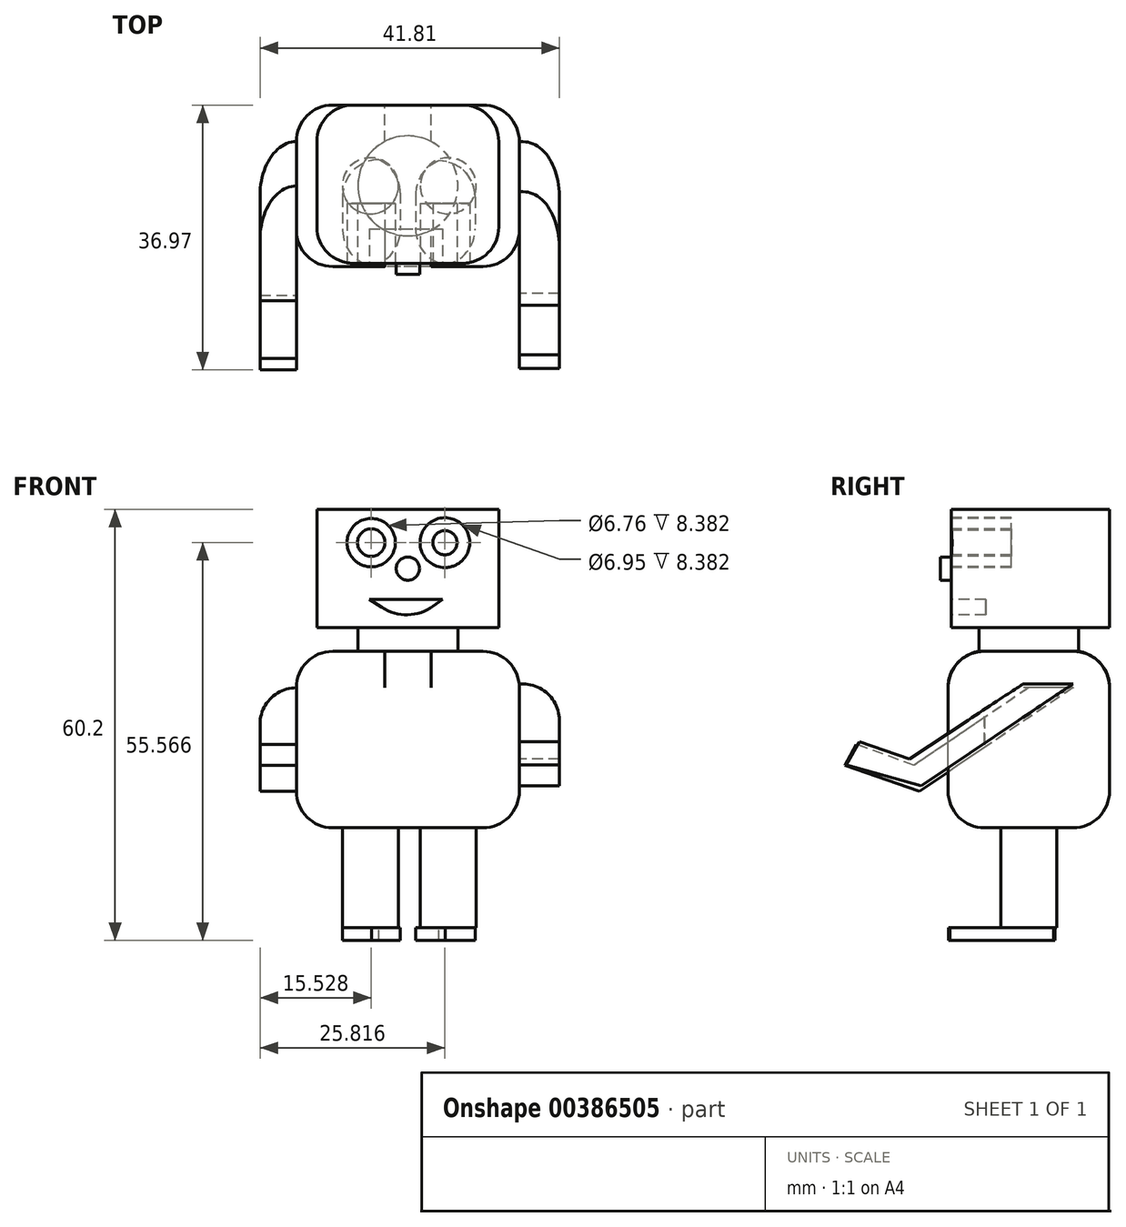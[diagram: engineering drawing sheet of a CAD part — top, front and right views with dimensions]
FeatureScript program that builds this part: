
annotation { "Feature Type Name" : "Feature", "Feature Type Description" : "" }
export const myFeature = defineFeature(function(context is Context, id is Id, definition is map)
    precondition{}
    {
        {
            var Q0;
            Q0=qCreatedBy(makeId("Front.planeOp"),FACE);
            var sketch = newSketch(context, id + "F0", { "sketchPlane" : qUnion([Q0])});
            skLineSegment(sketch, "E0.bottom", {"start": v(12.7, -8.26) * mm, "end": v(-12.7, -8.26) * mm});
            skLineSegment(sketch, "E0.top", {"start": v(12.7, 8.26) * mm, "end": v(-12.7, 8.26) * mm});
            skLineSegment(sketch, "E0.left", {"start": v(12.7, -8.26) * mm, "end": v(12.7, 8.26) * mm});
            skLineSegment(sketch, "E0.right", {"start": v(-12.7, -8.26) * mm, "end": v(-12.7, 8.26) * mm});
            skPoint(sketch, "E0.middle", {"position": v(0, 0) * mm});
            skSolve(sketch);
        }
        {
            var Q0;
            Q0 = qSketchRegion(id + "F0", true);
            extrude(context, id + "F1", {"entities" : qUnion([Q0]), "depth" : 22.1 * mm});
        }
        {
            var Q0;
            Q0=makeQuery(id+"F1.opExtrude","CAP_EDGE",EDGE,{"disambiguationData":[OSD([sQuery(id+"F0.wireOp",EDGE,"E0.right")])],"isStart":false});
            var Q1;
            Q1=makeQuery(id+"F1.opExtrude","CAP_EDGE",EDGE,{"disambiguationData":[OSD([sQuery(id+"F0.wireOp",EDGE,"E0.left")])],"isStart":false});
            var Q2;
            Q2=makeQuery(id+"F1.opExtrude","CAP_EDGE",EDGE,{"disambiguationData":[OSD([sQuery(id+"F0.wireOp",EDGE,"E0.right")])],"isStart":true});
            var Q3;
            Q3=makeQuery(id+"F1.opExtrude","CAP_EDGE",EDGE,{"disambiguationData":[OSD([sQuery(id+"F0.wireOp",EDGE,"E0.left")])],"isStart":true});
            fillet(context, id + "F2", {"entities" : qUnion([Q0, Q1, Q2, Q3]), "radius" : 5.08 * mm, "tangentPropagation" : true, "allowEdgeOverflow" : false});
        }
        {
            var Q0;
            Q0=makeQuery(id+"F1.opExtrude","SWEPT_FACE",FACE,{"disambiguationData":[OSD([sQuery(id+"F0.wireOp",EDGE,"E0.bottom")])]});
            var sketch = newSketch(context, id + "F3", { "sketchPlane" : qUnion([Q0])});
            skCircle(sketch, "E1", {"center": v(0, 11.27) * mm, "radius": 6.98 * mm});
            skSolve(sketch);
        }
        {
            var Q0;
            Q0 = qSketchRegion(id + "F3", true);
            extrude(context, id + "F4", {"entities" : qUnion([Q0]), "operationType" : NewBodyOperationType.ADD, "depth" : 3.3 * mm});
        }
        {
            var Q0;
            Q0=makeQuery(id+"F4.opExtrude","CAP_FACE",FACE,{"disambiguationData":[OSD([sQuery(id+"F3.wireOp",EDGE,"E1")])],"isStart":false});
            var sketch = newSketch(context, id + "F5", { "sketchPlane" : qUnion([Q0])});
            skLineSegment(sketch, "E2.bottom", {"start": v(15.57, 0) * mm, "end": v(-15.57, 0) * mm});
            skLineSegment(sketch, "E2.top", {"start": v(15.57, 22.55) * mm, "end": v(-15.57, 22.55) * mm});
            skLineSegment(sketch, "E2.left", {"start": v(15.57, 0) * mm, "end": v(15.57, 22.55) * mm});
            skLineSegment(sketch, "E2.right", {"start": v(-15.57, 0) * mm, "end": v(-15.57, 22.55) * mm});
            skPoint(sketch, "E2.middle", {"position": v(0, 11.27) * mm});
            skSolve(sketch);
        }
        {
            var Q0;
            Q0 = qSketchRegion(id + "F5", true);
            extrude(context, id + "F6", {"entities" : qUnion([Q0]), "operationType" : NewBodyOperationType.ADD, "depth" : 24.64 * mm});
        }
        {
            var Q0;
            Q0=makeQuery(id+"F6.opExtrude","SWEPT_EDGE",EDGE,{"disambiguationData":[OSD([sQuery(id+"F5.wireOp",EDGE,"E2.top"),sQuery(id+"F5.wireOp",EDGE,"E2.left")])]});
            var Q1;
            Q1=makeQuery(id+"F6.opExtrude","SWEPT_EDGE",EDGE,{"disambiguationData":[OSD([sQuery(id+"F5.wireOp",EDGE,"E2.top"),sQuery(id+"F5.wireOp",EDGE,"E2.right")])]});
            var Q2;
            Q2=makeQuery(id+"F6.opExtrude","SWEPT_EDGE",EDGE,{"disambiguationData":[OSD([sQuery(id+"F5.wireOp",EDGE,"E2.bottom"),sQuery(id+"F5.wireOp",EDGE,"E2.left")])]});
            var Q3;
            Q3=makeQuery(id+"F6.opExtrude","SWEPT_EDGE",EDGE,{"disambiguationData":[OSD([sQuery(id+"F5.wireOp",EDGE,"E2.bottom"),sQuery(id+"F5.wireOp",EDGE,"E2.right")])]});
            var Q4;
            Q4=makeQuery(id+"F6.opExtrude","CAP_EDGE",EDGE,{"disambiguationData":[OSD([sQuery(id+"F5.wireOp",EDGE,"E2.left")])],"isStart":true});
            var Q5;
            Q5=makeQuery(id+"F6.opExtrude","CAP_EDGE",EDGE,{"disambiguationData":[OSD([sQuery(id+"F5.wireOp",EDGE,"E2.bottom")])],"isStart":true});
            var Q6;
            Q6=makeQuery(id+"F6.opExtrude","SWEPT_FACE",FACE,{"disambiguationData":[OSD([sQuery(id+"F5.wireOp",EDGE,"E2.top")])]});
            var Q7;
            Q7=makeQuery(id+"F6.opExtrude","CAP_EDGE",EDGE,{"disambiguationData":[OSD([sQuery(id+"F5.wireOp",EDGE,"E2.top")])],"isStart":false});
            var Q8;
            Q8=makeQuery(id+"F6.opExtrude","CAP_EDGE",EDGE,{"disambiguationData":[OSD([sQuery(id+"F5.wireOp",EDGE,"E2.right")])],"isStart":false});
            var Q9;
            Q9=makeQuery(id+"F6.opExtrude","CAP_EDGE",EDGE,{"disambiguationData":[OSD([sQuery(id+"F5.wireOp",EDGE,"E2.bottom")])],"isStart":false});
            var Q10;
            Q10=makeQuery(id+"F6.opExtrude","CAP_EDGE",EDGE,{"disambiguationData":[OSD([sQuery(id+"F5.wireOp",EDGE,"E2.left")])],"isStart":false});
            var Q11;
            Q11=makeQuery(id+"F6.opExtrude","CAP_EDGE",EDGE,{"disambiguationData":[OSD([sQuery(id+"F5.wireOp",EDGE,"E2.right")])],"isStart":true});
            fillet(context, id + "F7", {"entities" : qUnion([Q0, Q1, Q2, Q3, Q4, Q5, Q6, Q7, Q8, Q9, Q10, Q11]), "radius" : 5.08 * mm, "tangentPropagation" : true, "allowEdgeOverflow" : false});
        }
        {
            var Q0;
            Q0=makeQuery(id+"F6.opExtrude","SWEPT_FACE",FACE,{"disambiguationData":[OSD([sQuery(id+"F5.wireOp",EDGE,"E2.left")])]});
            var sketch = newSketch(context, id + "F8", { "sketchPlane" : qUnion([Q0])});
            skLineSegment(sketch, "E3", {"start": v(-11.27, -16.64) * mm, "end": v(-27.42, -27.24) * mm});
            skLineSegment(sketch, "E4", {"start": v(-5.08, -16.64) * mm, "end": v(-27.13, -31.12) * mm});
            skSolve(sketch);
        }
        {
            var Q0;
            Q0=makeQuery(id+"F6.opExtrude","SWEPT_FACE",FACE,{"disambiguationData":[OSD([sQuery(id+"F5.wireOp",EDGE,"E2.right")])]});
            var sketch = newSketch(context, id + "F9", { "sketchPlane" : qUnion([Q0])});
            skLineSegment(sketch, "E5", {"start": v(11.27, -16.64) * mm, "end": v(27.3, -27.49) * mm});
            skLineSegment(sketch, "E6", {"start": v(5.08, -16.64) * mm, "end": v(26.53, -31.11) * mm});
            skLineSegment(sketch, "E7", {"start": v(27.3, -27.49) * mm, "end": v(35.36, -24.53) * mm});
            skLineSegment(sketch, "E8", {"start": v(26.53, -31.11) * mm, "end": v(36.97, -27.49) * mm});
            skLineSegment(sketch, "E9", {"start": v(35.36, -24.53) * mm, "end": v(36.97, -27.49) * mm});
            skLineSegment(sketch, "E10", {"start": v(5.08, -16.64) * mm, "end": v(11.27, -16.64) * mm});
            skLineSegment(sketch, "E11", {"start": v(11.17, -17.28) * mm, "end": v(5.08, -16.64) * mm});
            skSolve(sketch);
        }
        {
            var Q0;
            Q0 = qSketchRegion(id + "F9", true);
            extrude(context, id + "F10", {"entities" : qUnion([Q0]), "operationType" : NewBodyOperationType.ADD, "depth" : 5.08 * mm});
        }
        {
            var Q0;
            Q0=makeQuery(id+"F10.opExtrude","CAP_EDGE",EDGE,{"disambiguationData":[OSD([sQuery(id+"F9.wireOp",EDGE,"E10")])],"isStart":false});
            fillet(context, id + "F11", {"entities" : qUnion([Q0]), "radius" : 5.08 * mm, "tangentPropagation" : true, "allowEdgeOverflow" : false});
        }
        {
            var Q0;
            {var subQ1=sQuery(id+"F5.wireOp",EDGE,"E2.left");var subQ2=makeQuery(id+"F6.opExtrude","SWEPT_FACE",FACE,{"disambiguationData":[OSD([subQ1])]});var subQ6=makeQuery(id+"F7.opFillet","BLEND_EDGE",EDGE,{"blendedFrom":[makeQuery(id+"F6.opExtrude","CAP_EDGE",EDGE,{"disambiguationData":[OSD([subQ1])],"isStart":false}),subQ2],"blendedInto":[subQ2]});Q0=makeQuery(id+"F8.imprint","IMPRINT",FACE,{"disambiguationData":[TD([[makeQuery(id+"F8.imprint","IMPRINT",EDGE,{"derivedFrom":subQ6}),1.0]])]});}
            var sketch = newSketch(context, id + "F12", { "sketchPlane" : qUnion([Q0])});
            skLineSegment(sketch, "E12", {"start": v(-5.1, -16.11) * mm, "end": v(-26.31, -30.34) * mm});
            skLineSegment(sketch, "E13", {"start": v(-12.08, -16.11) * mm, "end": v(-27.92, -26.58) * mm});
            skLineSegment(sketch, "E14", {"start": v(-12.08, -16.11) * mm, "end": v(-5.1, -16.11) * mm});
            skLineSegment(sketch, "E15", {"start": v(-27.92, -26.58) * mm, "end": v(-34.9, -24.17) * mm});
            skLineSegment(sketch, "E16", {"start": v(-26.31, -30.34) * mm, "end": v(-36.78, -27.39) * mm});
            skLineSegment(sketch, "E17", {"start": v(-36.78, -27.39) * mm, "end": v(-34.9, -24.17) * mm});
            skSolve(sketch);
        }
        {
            var Q0;
            Q0 = qSketchRegion(id + "F12", true);
            extrude(context, id + "F13", {"entities" : qUnion([Q0]), "operationType" : NewBodyOperationType.ADD, "depth" : 5.6 * mm});
        }
        {
            var Q0;
            Q0=makeQuery(id+"F13.opExtrude","CAP_EDGE",EDGE,{"disambiguationData":[OSD([sQuery(id+"F12.wireOp",EDGE,"E14")])],"isStart":false});
            fillet(context, id + "F14", {"entities" : qUnion([Q0]), "radius" : 5.08 * mm, "tangentPropagation" : true, "allowEdgeOverflow" : false});
        }
        {
            var Q0;
            Q0=makeQuery(id+"F6.opExtrude","CAP_FACE",FACE,{"disambiguationData":[OSD([sQuery(id+"F5.wireOp",EDGE,"E2.bottom"),sQuery(id+"F5.wireOp",EDGE,"E2.top"),sQuery(id+"F5.wireOp",EDGE,"E2.left"),sQuery(id+"F5.wireOp",EDGE,"E2.right")])],"isStart":false});
            var sketch = newSketch(context, id + "F15", { "sketchPlane" : qUnion([Q0])});
            skCircle(sketch, "E18", {"center": v(5.64, 11.27) * mm, "radius": 3.9 * mm});
            skPoint(sketch, "E18.centerSnap0", {"position": v(10.5, 11.27) * mm});
            skPoint(sketch, "E19.centerSnap0", {"position": v(-10.5, 11.27) * mm});
            skCircle(sketch, "E20", {"center": v(-5.24, 11.27) * mm, "radius": 3.92 * mm});
            skSolve(sketch);
        }
        {
            var Q0;
            Q0 = qSketchRegion(id + "F15", true);
            extrude(context, id + "F16", {"entities" : qUnion([Q0]), "operationType" : NewBodyOperationType.ADD, "depth" : 13.97 * mm});
        }
        {
            var Q0;
            Q0=makeQuery(id+"F16.opExtrude","CAP_FACE",FACE,{"disambiguationData":[OSD([sQuery(id+"F15.wireOp",EDGE,"E18")])],"isStart":false});
            var sketch = newSketch(context, id + "F17", { "sketchPlane" : qUnion([Q0])});
            skLineSegment(sketch, "E21.bottom", {"start": v(-9.11, 7.63) * mm, "end": v(-1.07, 7.63) * mm});
            skLineSegment(sketch, "E21.top", {"start": v(-9.11, 22.57) * mm, "end": v(-1.07, 22.57) * mm});
            skLineSegment(sketch, "E21.left", {"start": v(-9.11, 7.63) * mm, "end": v(-9.11, 22.57) * mm});
            skLineSegment(sketch, "E21.right", {"start": v(-1.07, 7.63) * mm, "end": v(-1.07, 22.57) * mm});
            skLineSegment(sketch, "E22.bottom", {"start": v(1.07, 7.78) * mm, "end": v(9.4, 7.78) * mm});
            skLineSegment(sketch, "E22.top", {"start": v(1.07, 22.38) * mm, "end": v(9.4, 22.38) * mm});
            skLineSegment(sketch, "E22.left", {"start": v(1.07, 7.78) * mm, "end": v(1.07, 22.38) * mm});
            skLineSegment(sketch, "E22.right", {"start": v(9.4, 7.78) * mm, "end": v(9.4, 22.38) * mm});
            skSolve(sketch);
        }
        {
            var Q0;
            Q0 = qSketchRegion(id + "F17", true);
            extrude(context, id + "F18", {"entities" : qUnion([Q0]), "operationType" : NewBodyOperationType.ADD, "depth" : 1.78 * mm});
        }
        {
            var Q0;
            Q0=makeQuery(id+"F18.opExtrude","SWEPT_EDGE",EDGE,{"disambiguationData":[OSD([sQuery(id+"F17.wireOp",EDGE,"E22.bottom"),sQuery(id+"F17.wireOp",EDGE,"E22.right")])]});
            fillet(context, id + "F19", {"entities" : qUnion([Q0]), "radius" : 5.08 * mm, "tangentPropagation" : true, "allowEdgeOverflow" : false});
        }
        {
            var Q0;
            Q0=makeQuery(id+"F18.opExtrude","SWEPT_EDGE",EDGE,{"disambiguationData":[OSD([sQuery(id+"F17.wireOp",EDGE,"E21.bottom"),sQuery(id+"F17.wireOp",EDGE,"E21.left")])]});
            fillet(context, id + "F20", {"entities" : qUnion([Q0]), "radius" : 5.08 * mm, "tangentPropagation" : true, "allowEdgeOverflow" : false});
        }
        {
            var Q0;
            Q0=makeQuery(id+"F1.opExtrude","CAP_FACE",FACE,{"disambiguationData":[OSD([sQuery(id+"F0.wireOp",EDGE,"E0.bottom"),sQuery(id+"F0.wireOp",EDGE,"E0.top"),sQuery(id+"F0.wireOp",EDGE,"E0.left"),sQuery(id+"F0.wireOp",EDGE,"E0.right")])],"isStart":false});
            var sketch = newSketch(context, id + "F21", { "sketchPlane" : qUnion([Q0])});
            skSolve(sketch);
        }
        {
            var Q0;
            {var subQ0=sQuery(id+"F0.wireOp",EDGE,"E0.bottom");Q0=makeQuery(id+"F21.imprint","IMPRINT",FACE,{"disambiguationData":[TD([[makeQuery(id+"F21.imprint","IMPRINT",EDGE,{"derivedFrom":makeQuery(id+"F1.opExtrude","CAP_EDGE",EDGE,{"disambiguationData":[OSD([subQ0])],"isStart":false})}),-1.0]])]});}
            var sketch = newSketch(context, id + "F22", { "sketchPlane" : qUnion([Q0])});
            skCircle(sketch, "E23", {"center": v(5.17, 3.63) * mm, "radius": 3.47 * mm});
            skCircle(sketch, "E24", {"center": v(-5.12, 3.63) * mm, "radius": 3.38 * mm});
            skCircle(sketch, "E25", {"center": v(5.17, 3.63) * mm, "radius": 1.7 * mm});
            skCircle(sketch, "E26", {"center": v(-5.12, 3.63) * mm, "radius": 1.92 * mm});
            skSolve(sketch);
        }
        {
            var Q0;
            Q0 = qSketchRegion(id + "F22", true);
            extrude(context, id + "F23", {"entities" : qUnion([Q0]), "operationType" : NewBodyOperationType.REMOVE, "oppositeDirection" : true, "depth" : 8.38 * mm});
        }
        {
            var Q0;
            {var subQ0=sQuery(id+"F0.wireOp",EDGE,"E0.bottom");Q0=makeQuery(id+"F21.imprint","IMPRINT",FACE,{"disambiguationData":[TD([[makeQuery(id+"F21.imprint","IMPRINT",EDGE,{"derivedFrom":makeQuery(id+"F1.opExtrude","CAP_EDGE",EDGE,{"disambiguationData":[OSD([subQ0])],"isStart":false})}),-1.0]])]});}
            var sketch = newSketch(context, id + "F24", { "sketchPlane" : qUnion([Q0])});
            skCircle(sketch, "E27", {"center": v(0, 0) * mm, "radius": 1.63 * mm});
            skSolve(sketch);
        }
        {
            var Q0;
            Q0 = qSketchRegion(id + "F24", true);
            extrude(context, id + "F25", {"entities" : qUnion([Q0]), "operationType" : NewBodyOperationType.ADD, "depth" : 1.52 * mm});
        }
        {
            var Q0;
            Q0=makeQuery(id+"F18.opExtrude","SWEPT_EDGE",EDGE,{"disambiguationData":[OSD([sQuery(id+"F17.wireOp",EDGE,"E21.bottom"),sQuery(id+"F17.wireOp",EDGE,"E21.right")])]});
            var Q1;
            Q1=makeQuery(id+"F18.opExtrude","SWEPT_EDGE",EDGE,{"disambiguationData":[OSD([sQuery(id+"F17.wireOp",EDGE,"E22.bottom"),sQuery(id+"F17.wireOp",EDGE,"E22.left")])]});
            fillet(context, id + "F26", {"entities" : qUnion([Q0, Q1]), "radius" : 5.08 * mm, "tangentPropagation" : true, "allowEdgeOverflow" : false});
        }
        {
            var Q0;
            {var subQ0=sQuery(id+"F0.wireOp",EDGE,"E0.bottom");Q0=makeQuery(id+"F21.imprint","IMPRINT",FACE,{"disambiguationData":[TD([[makeQuery(id+"F21.imprint","IMPRINT",EDGE,{"derivedFrom":makeQuery(id+"F1.opExtrude","CAP_EDGE",EDGE,{"disambiguationData":[OSD([subQ0])],"isStart":false})}),-1.0]])]});}
            var sketch = newSketch(context, id + "F27", { "sketchPlane" : qUnion([Q0])});
            skLineSegment(sketch, "E28", {"start": v(-5.37, -4.3) * mm, "end": v(4.83, -4.3) * mm});
            skLineSegment(sketch, "E29", {"start": v(-5.37, -4.3) * mm, "end": v(-3.65, -5.42) * mm});
            skLineSegment(sketch, "E30", {"start": v(3.53, -5.24) * mm, "end": v(4.83, -4.3) * mm});
            skPoint(sketch, "E31.visualSharp", {"position": v(0, -7.79) * mm});
            skArc(sketch, "E31.filletArc", {"start": v(-3.65, -5.42) * mm, "mid": v(-0.03, -6.44) * mm, "end": v(3.53, -5.24) * mm});
            skSolve(sketch);
        }
        {
            var Q0;
            Q0 = qSketchRegion(id + "F27", true);
            extrude(context, id + "F28", {"entities" : qUnion([Q0]), "operationType" : NewBodyOperationType.REMOVE, "oppositeDirection" : true, "depth" : 4.83 * mm});
        }
        {
            var Q0;
            Q0=makeQuery(id+"F18.opExtrude","SWEPT_EDGE",EDGE,{"disambiguationData":[OSD([sQuery(id+"F17.wireOp",EDGE,"E21.top"),sQuery(id+"F17.wireOp",EDGE,"E21.left")])]});
            var Q1;
            Q1=makeQuery(id+"F18.opExtrude","SWEPT_EDGE",EDGE,{"disambiguationData":[OSD([sQuery(id+"F17.wireOp",EDGE,"E21.top"),sQuery(id+"F17.wireOp",EDGE,"E21.right")])]});
            var Q2;
            Q2=makeQuery(id+"F18.opExtrude","SWEPT_EDGE",EDGE,{"disambiguationData":[OSD([sQuery(id+"F17.wireOp",EDGE,"E22.top"),sQuery(id+"F17.wireOp",EDGE,"E22.right")])]});
            var Q3;
            Q3=makeQuery(id+"F18.opExtrude","SWEPT_EDGE",EDGE,{"disambiguationData":[OSD([sQuery(id+"F17.wireOp",EDGE,"E22.top"),sQuery(id+"F17.wireOp",EDGE,"E22.left")])]});
            fillet(context, id + "F29", {"entities" : qUnion([Q0, Q1, Q2, Q3]), "radius" : 5.08 * mm, "tangentPropagation" : true, "allowEdgeOverflow" : false});
        }
    });
